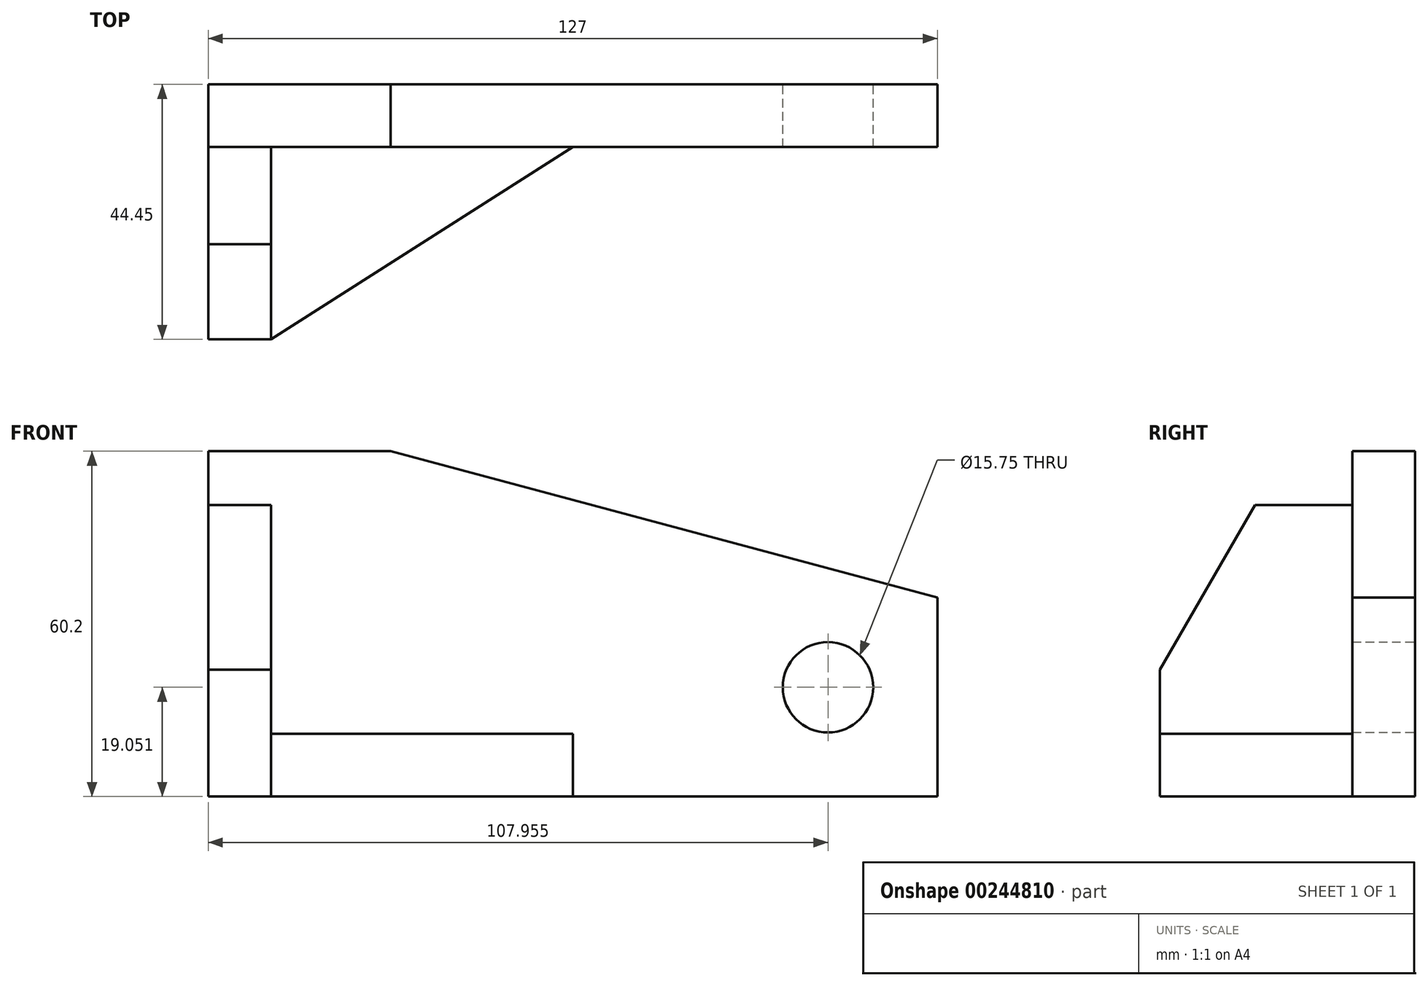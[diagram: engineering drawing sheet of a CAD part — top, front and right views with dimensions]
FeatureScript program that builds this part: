
annotation { "Feature Type Name" : "Feature", "Feature Type Description" : "" }
export const myFeature = defineFeature(function(context is Context, id is Id, definition is map)
    precondition{}
    {
        {
            var Q0;
            Q0=qCreatedBy(makeId("Front.planeOp"),FACE);
            var sketch = newSketch(context, id + "F0", { "sketchPlane" : qUnion([Q0])});
            skLineSegment(sketch, "E0.bottom", {"start": v(15.87, 30.1) * mm, "end": v(-15.88, 30.1) * mm});
            skLineSegment(sketch, "E0.top", {"start": v(15.88, -30.1) * mm, "end": v(-15.87, -30.1) * mm});
            skLineSegment(sketch, "E0.left", {"start": v(15.87, 30.1) * mm, "end": v(15.88, -30.1) * mm});
            skLineSegment(sketch, "E0.right", {"start": v(-15.88, 30.1) * mm, "end": v(-15.87, -30.1) * mm});
            skPoint(sketch, "E0.middle", {"position": v(0, 0) * mm});
            skLineSegment(sketch, "E1", {"start": v(15.87, 30.1) * mm, "end": v(111.12, 4.58) * mm});
            skLineSegment(sketch, "E2", {"start": v(111.12, 4.58) * mm, "end": v(111.12, -44.6) * mm});
            skLineSegment(sketch, "E3", {"start": v(15.88, -30.1) * mm, "end": v(111.12, -30.1) * mm});
            skCircle(sketch, "E4", {"center": v(92.08, -11.05) * mm, "radius": 7.87 * mm});
            skSolve(sketch);
        }
        {
            var Q0;
            Q0 = qSketchRegion(id + "F0", true);
            extrude(context, id + "F1", {"entities" : qUnion([Q0]), "depth" : 10.92 * mm});
        }
        {
            var Q0;
            Q0=makeQuery(id+"F1.opExtrude","SWEPT_FACE",FACE,{"disambiguationData":[OSD([sQuery(id+"F0.wireOp",EDGE,"E0.top"),sQuery(id+"F0.wireOp",EDGE,"E3")])]});
            var sketch = newSketch(context, id + "F2", { "sketchPlane" : qUnion([Q0])});
            skLineSegment(sketch, "E5", {"start": v(-15.87, 10.92) * mm, "end": v(-15.87, 44.45) * mm});
            skLineSegment(sketch, "E6", {"start": v(-4.95, 10.92) * mm, "end": v(-4.95, 44.45) * mm});
            skLineSegment(sketch, "E7", {"start": v(-15.87, 44.45) * mm, "end": v(-4.95, 44.45) * mm});
            skLineSegment(sketch, "E8", {"start": v(-4.95, 44.45) * mm, "end": v(47.62, 10.92) * mm});
            skSolve(sketch);
        }
        {
            var Q0;
            {var subQ0=sQuery(id+"F2.wireOp",EDGE,"E6");Q0=makeQuery(id+"F2.imprint","IMPRINT",FACE,{"disambiguationData":[TD([[makeQuery(id+"F2.imprint","IMPRINT",EDGE,{"derivedFrom":subQ0}),-1.0]])]});}
            extrude(context, id + "F3", {"entities" : qUnion([Q0]), "operationType" : NewBodyOperationType.ADD, "oppositeDirection" : true, "depth" : 10.92 * mm});
        }
        {
            var Q0;
            {var subQ0=sQuery(id+"F2.wireOp",EDGE,"E5");Q0=makeQuery(id+"F2.imprint","IMPRINT",FACE,{"disambiguationData":[TD([[makeQuery(id+"F2.imprint","IMPRINT",EDGE,{"derivedFrom":subQ0}),-1.0]])]});}
            extrude(context, id + "F4", {"entities" : qUnion([Q0]), "operationType" : NewBodyOperationType.ADD, "oppositeDirection" : true, "depth" : 22.1 * mm});
        }
        {
            var Q0;
            Q0=makeQuery(id+"F4.boolean.opBoolean","MERGE",FACE,{"derivedFrom":[makeQuery(id+"F1.opExtrude","SWEPT_FACE",FACE,{"disambiguationData":[OSD([sQuery(id+"F0.wireOp",EDGE,"E0.right")])]}),makeQuery(id+"F4.opExtrude","SWEPT_FACE",FACE,{"disambiguationData":[OSD([sQuery(id+"F2.wireOp",EDGE,"E5")])]})]});
            var sketch = newSketch(context, id + "F5", { "sketchPlane" : qUnion([Q0])});
            skLineSegment(sketch, "E9", {"start": v(44.45, -8) * mm, "end": v(44.45, 28.17) * mm, "construction": true});
            skLineSegment(sketch, "E10", {"start": v(44.45, -8) * mm, "end": v(27.88, 20.7) * mm});
            skLineSegment(sketch, "E11", {"start": v(27.88, 20.7) * mm, "end": v(10.92, 20.7) * mm});
            skSolve(sketch);
        }
        {
            var Q0;
            Q0=makeQuery(id+"F5.imprint","IMPRINT",FACE,{"disambiguationData":[TD([[makeQuery(id+"F5.imprint","IMPRINT",EDGE,{"derivedFrom":sQuery(id+"F5.wireOp",EDGE,"E10")}),1.0]])]});
            extrude(context, id + "F6", {"entities" : qUnion([Q0]), "operationType" : NewBodyOperationType.ADD, "oppositeDirection" : true, "depth" : 10.92 * mm});
        }
    });
